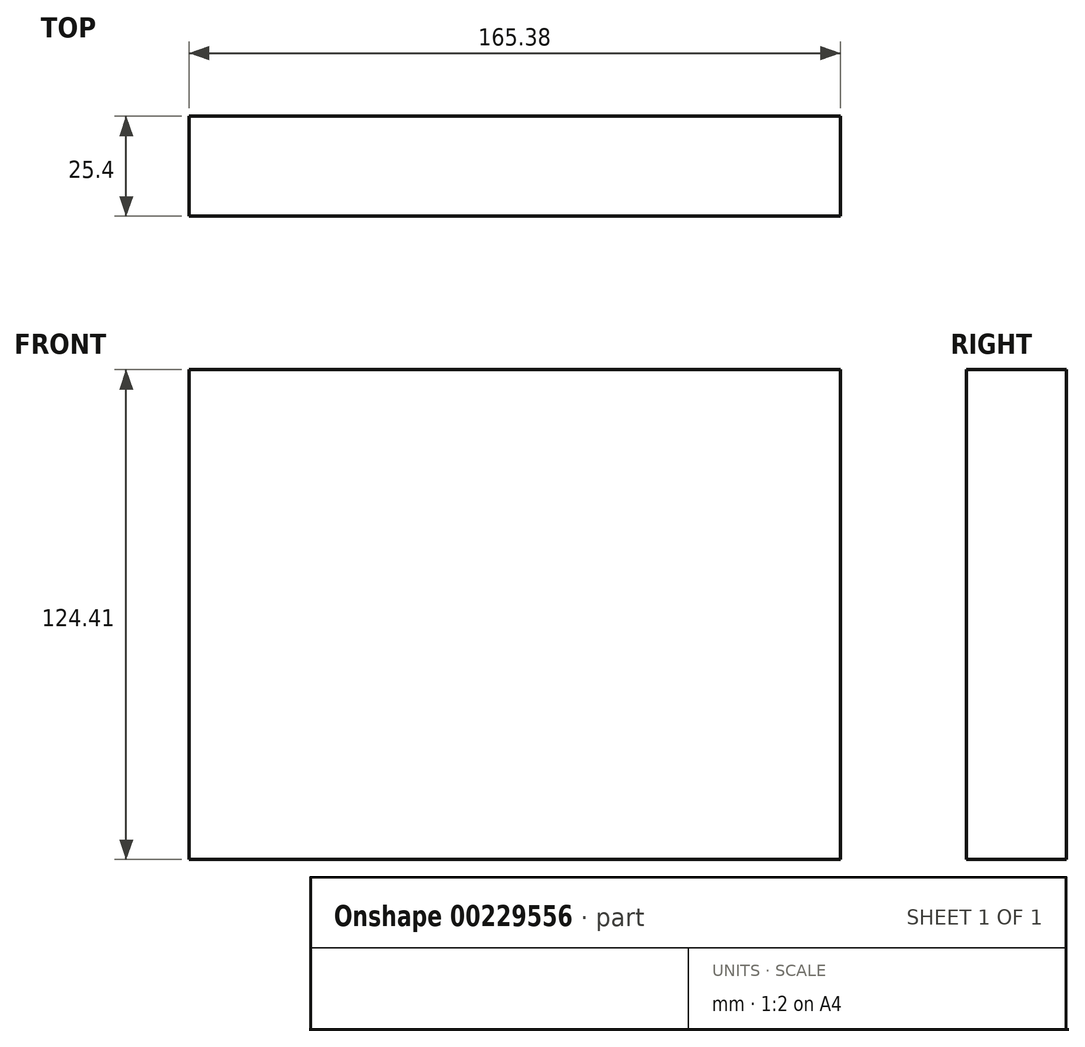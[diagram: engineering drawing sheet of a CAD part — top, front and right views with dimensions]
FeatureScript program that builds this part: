
annotation { "Feature Type Name" : "Feature", "Feature Type Description" : "" }
export const myFeature = defineFeature(function(context is Context, id is Id, definition is map)
    precondition{}
    {
        {
            var Q0;
            Q0=qCreatedBy(makeId("Front.planeOp"),FACE);
            var sketch = newSketch(context, id + "F0", { "sketchPlane" : qUnion([Q0])});
            skLineSegment(sketch, "E0.bottom", {"start": v(-94.14, 59.96) * mm, "end": v(71.24, 59.96) * mm});
            skLineSegment(sketch, "E0.top", {"start": v(-94.14, -64.45) * mm, "end": v(71.24, -64.45) * mm});
            skLineSegment(sketch, "E0.left", {"start": v(-94.14, 59.96) * mm, "end": v(-94.14, -64.45) * mm});
            skLineSegment(sketch, "E0.right", {"start": v(71.24, 59.96) * mm, "end": v(71.24, -64.45) * mm});
            skSolve(sketch);
        }
        {
            var Q0;
            Q0 = qSketchRegion(id + "F0", true);
            extrude(context, id + "F1", {"entities" : qUnion([Q0]), "depth" : 25.4 * mm});
        }
    });
